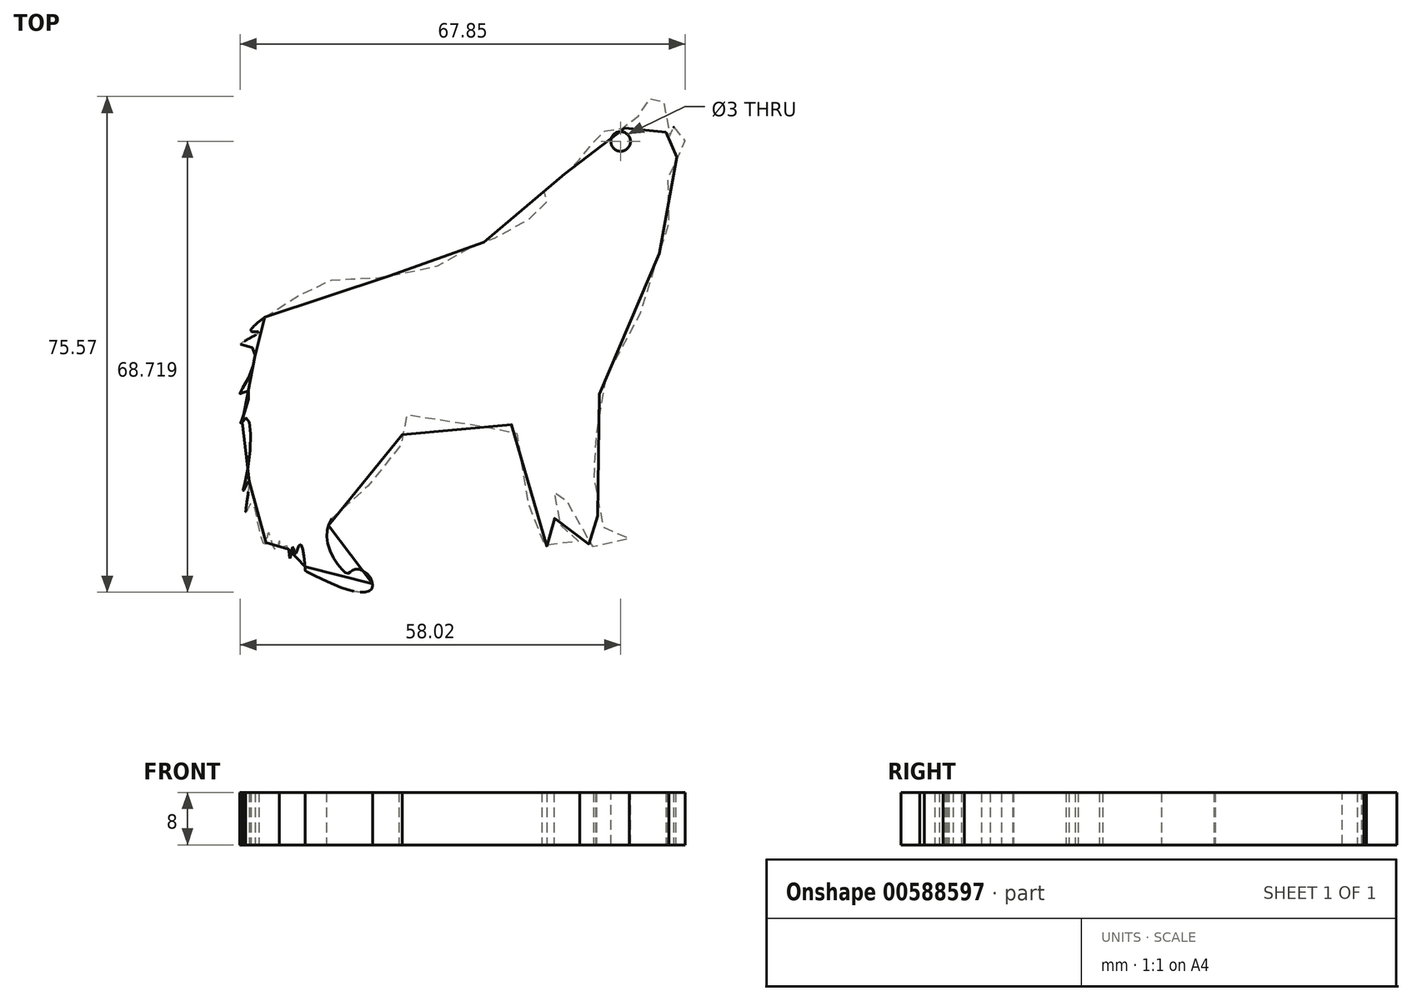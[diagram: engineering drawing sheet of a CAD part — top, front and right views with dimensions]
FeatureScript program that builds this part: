
annotation { "Feature Type Name" : "Feature", "Feature Type Description" : "" }
export const myFeature = defineFeature(function(context is Context, id is Id, definition is map)
    precondition{}
    {
        {
            var Q0;
            Q0=qCreatedBy(makeId("Top.planeOp"),FACE);
            var sketch = newSketch(context, id + "F0", { "sketchPlane" : qUnion([Q0])});
            skFitSpline(sketch, "E0", {"points": [v(-64.06, 41.81) * mm, v(-53.17, 47.7) * mm, v(-49.79, 47.57) * mm, v(-39.64, 49.2) * mm, v(-36.76, 50.08) * mm, v(-33.13, 52.33) * mm, v(-28.62, 54.08) * mm, v(-21.1, 59.35) * mm, v(-21.86, 60.35) * mm, v(-16.97, 64.73) * mm, v(-16.03, 65.97) * mm, v(-13.42, 69.1) * mm, v(-11.8, 70.36) * mm, v(-8.68, 70.89) * mm, v(-6, 74.39) * mm, v(-4.36, 75.46) * mm, v(-2.5, 72.67) * mm, v(-2.8, 69.47) * mm, v(-1.45, 70.29) * mm, v(-1.75, 70.81) * mm, v(-1.08, 70.44) * mm, v(-0.86, 70.59) * mm, v(0, 69.32) * mm, v(-1.75, 65.37) * mm, v(-2.87, 60.09) * mm, v(-2.57, 54.65) * mm, v(-4.06, 51.3) * mm, v(-6.74, 42.66) * mm, v(-13.11, 29.94) * mm, v(-13.53, 21.63) * mm, v(-13.94, 16.67) * mm, v(-12.35, 9.76) * mm, v(-10.05, 9.5) * mm, v(-8.54, 7.63) * mm, v(-13.34, 6.55) * mm, v(-17.42, 12.13) * mm, v(-19.63, 17) * mm, v(-19.9, 11.6) * mm, v(-19.45, 10.27) * mm, v(-17.5, 9.91) * mm, v(-16.09, 8.05) * mm, v(-18.83, 6.64) * mm, v(-21.93, 7.52) * mm, v(-23.97, 14.08) * mm, v(-26.19, 25.32) * mm, v(-28.84, 25.06) * mm, v(-43.37, 26.74) * mm, v(-43.1, 24) * mm, v(-46.38, 17.8) * mm, v(-52.2, 13.04) * mm, v(-54.57, 7.84) * mm, v(-51.47, 2.77) * mm, v(-50.72, 3.27) * mm, v(-48.6, 2.9) * mm, v(-47.72, 0.51) * mm, v(-50.22, 0) * mm, v(-55.54, 2.02) * mm, v(-57.86, 3.2) * mm, v(-57.92, 3.64) * mm, v(-58.68, 7.21) * mm, v(-59.36, 5.77) * mm, v(-59.74, 6.78) * mm, v(-60.05, 5.84) * mm, v(-60.24, 5.09) * mm, v(-60.74, 7.03) * mm, v(-61.74, 6.46) * mm, v(-61.8, 7.84) * mm, v(-62.43, 6.46) * mm, v(-63.5, 9.1) * mm, v(-63.94, 7.28) * mm, v(-64.62, 8.34) * mm, v(-66.13, 13.48) * mm, v(-66.94, 12.16) * mm, v(-66.44, 16.92) * mm, v(-67.32, 15.3) * mm, v(-66.44, 19.99) * mm, v(-66.94, 26.44) * mm, v(-67.77, 25.5) * mm, v(-66.5, 30.57) * mm, v(-67.77, 30.13) * mm, v(-66.57, 32.58) * mm, v(-66.07, 37.27) * mm, v(-67.77, 37.73) * mm, v(-64.94, 39.53) * mm, v(-66.07, 39.65) * mm, v(-64.06, 41.81) * mm]});
            skSolve(sketch);
        }
        {
            var Q0;
            Q0=makeQuery(id+"F0.imprint","IMPRINT",FACE,{"disambiguationData":[TD([[makeQuery(id+"F0.imprint","IMPRINT",EDGE,{"derivedFrom":sQuery(id+"F0.wireOp",EDGE,"E0")}),-1.0]])]});
            extrude(context, id + "F1", {"entities" : qUnion([Q0]), "depth" : 8 * mm, "offsetDistance" : 25 * mm});
        }
        {
            var Q0;
            Q0=makeQuery(id+"F1.opExtrude","CAP_FACE",FACE,{"disambiguationData":[OSD([sQuery(id+"F0.wireOp",EDGE,"E0")])],"isStart":false});
            var sketch = newSketch(context, id + "F2", { "sketchPlane" : qUnion([Q0])});
            skPoint(sketch, "E1", {"position": v(-9.82, 68.63) * mm});
            skSolve(sketch);
        }
        {
            var Q0;
            Q0=sQuery(id+"F2.wireOp",VERTEX,"E1");
            var Q1;
            Q1=makeQuery(id+"F1.opExtrude","SWEPT_BODY",BODY,{"disambiguationData":[OSD([sQuery(id+"F0.wireOp",EDGE,"E0")])]});
            hole(context, id + "F3", {"style" : HoleStyle.SIMPLE, "endStyle" : HoleEndStyle.THROUGH, "holeDiameter" : 3 * mm, "majorDiameter" : 5 * mm, "isTappedThrough" : true, "tappedDepth" : 12 * mm, "tapClearance" : 3, "locations" : qUnion([Q0]), "scope" : qUnion([Q1])});
        }
    });
